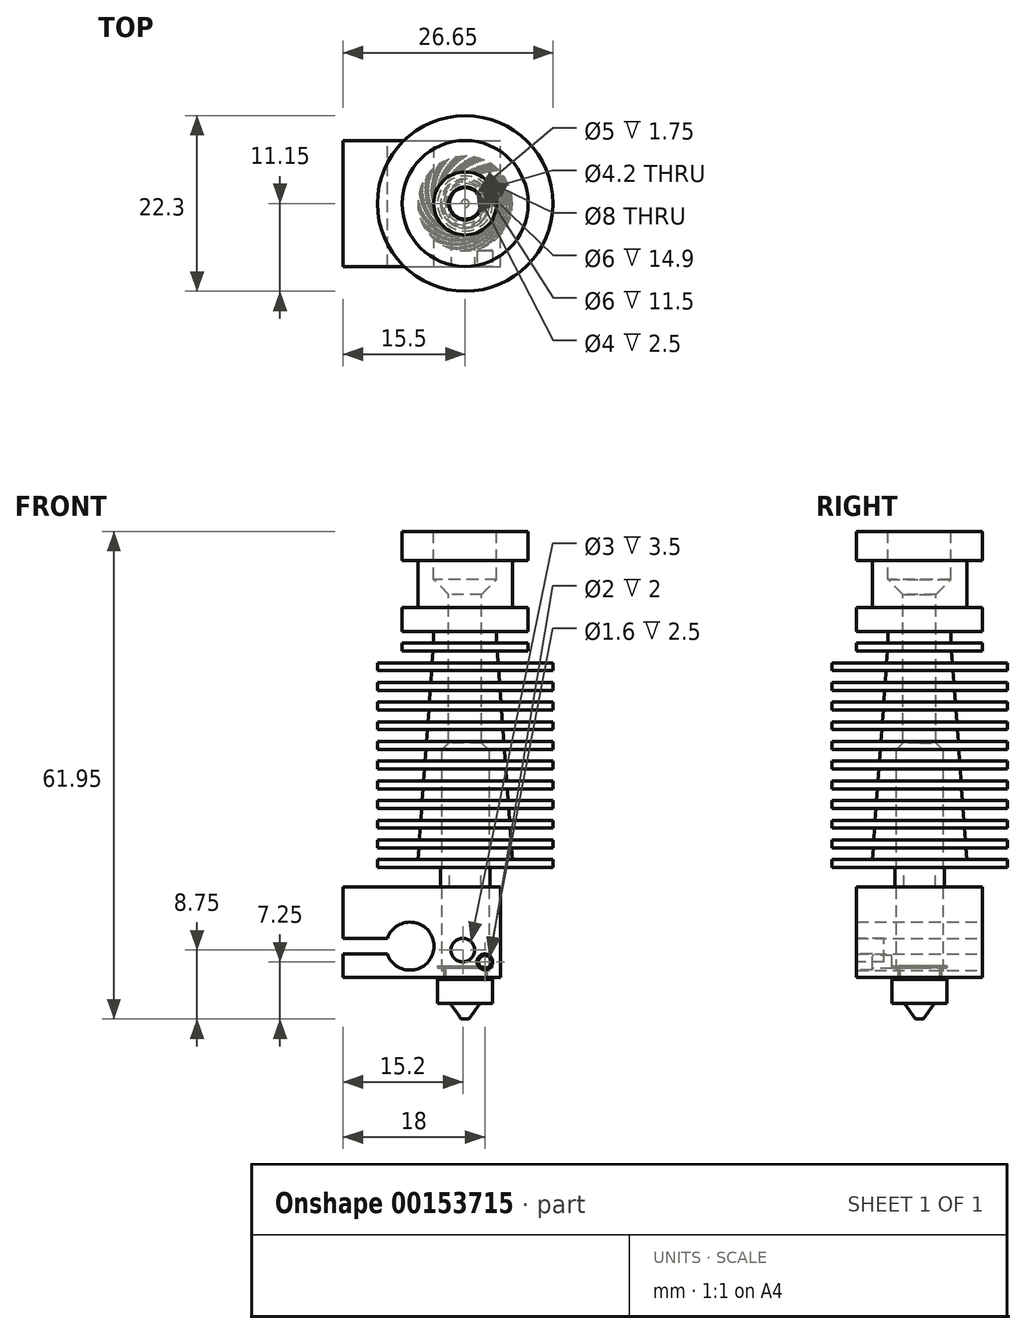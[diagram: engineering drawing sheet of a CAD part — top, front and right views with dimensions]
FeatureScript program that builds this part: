
annotation { "Feature Type Name" : "Feature", "Feature Type Description" : "" }
export const myFeature = defineFeature(function(context is Context, id is Id, definition is map)
    precondition{}
    {
        {
            var Q0;
            Q0=qCreatedBy(makeId("Top.planeOp"),FACE);
            var sketch = newSketch(context, id + "F0", { "sketchPlane" : qUnion([Q0])});
            skCircle(sketch, "E0", {"center": v(0, 0) * mm, "radius": 8 * mm});
            skSolve(sketch);
        }
        {
            var Q0;
            Q0=makeQuery(id+"F0.imprint","IMPRINT",FACE,{"disambiguationData":[TD([[makeQuery(id+"F0.imprint","IMPRINT",EDGE,{"derivedFrom":sQuery(id+"F0.wireOp",EDGE,"E0")}),1.0]])]});
            var Q1;
            Q1=sQuery(id+"F0.wireOp",EDGE,"E0");
            extrude(context, id + "F1", {"entities" : qUnion([Q0]), "surfaceEntities" : qUnion([Q1]), "oppositeDirection" : true, "depth" : 3.7 * mm});
        }
        {
            var Q0;
            Q0=makeQuery(id+"F1.opExtrude","CAP_FACE",FACE,{"disambiguationData":[OSD([sQuery(id+"F0.wireOp",EDGE,"E0")])],"isStart":false});
            var sketch = newSketch(context, id + "F2", { "sketchPlane" : qUnion([Q0])});
            skCircle(sketch, "E1", {"center": v(0, 0) * mm, "radius": 6 * mm});
            skSolve(sketch);
        }
        {
            var Q0;
            Q0=makeQuery(id+"F2.imprint","IMPRINT",FACE,{"disambiguationData":[TD([[makeQuery(id+"F2.imprint","IMPRINT",EDGE,{"derivedFrom":sQuery(id+"F2.wireOp",EDGE,"E1")}),1.0]])]});
            var Q1;
            Q1=sQuery(id+"F2.wireOp",EDGE,"E1");
            extrude(context, id + "F3", {"entities" : qUnion([Q0]), "operationType" : NewBodyOperationType.ADD, "surfaceEntities" : qUnion([Q1]), "depth" : 6 * mm});
        }
        {
            var Q0;
            Q0=makeQuery(id+"F3.opExtrude","CAP_FACE",FACE,{"disambiguationData":[OSD([sQuery(id+"F2.wireOp",EDGE,"E1")])],"isStart":false});
            var sketch = newSketch(context, id + "F4", { "sketchPlane" : qUnion([Q0])});
            skCircle(sketch, "E2", {"center": v(0, 0) * mm, "radius": 8 * mm});
            skSolve(sketch);
        }
        {
            var Q0;
            Q0=qSketchRegion(id+"F4",true);
            extrude(context, id + "F5", {"entities" : qUnion([Q0]), "operationType" : NewBodyOperationType.ADD, "depth" : 3 * mm});
        }
        {
            var Q0;
            Q0=qCreatedBy(makeId("Front.planeOp"),FACE);
            var sketch = newSketch(context, id + "F6", { "sketchPlane" : qUnion([Q0])});
            skLineSegment(sketch, "E3", {"start": v(0, 0) * mm, "end": v(0, -12.7) * mm});
            skLineSegment(sketch, "E4.bottom", {"start": v(0, -12.7) * mm, "end": v(4, -12.7) * mm});
            skLineSegment(sketch, "E4.top", {"start": v(0, -14.2) * mm, "end": v(4, -14.2) * mm});
            skLineSegment(sketch, "E4.left", {"start": v(0, -12.7) * mm, "end": v(0, -14.2) * mm});
            skLineSegment(sketch, "E4.right", {"start": v(4, -12.7) * mm, "end": v(4, -14.2) * mm});
            skLineSegment(sketch, "E5.bottom", {"start": v(0, -14.2) * mm, "end": v(8, -14.2) * mm});
            skLineSegment(sketch, "E5.top", {"start": v(0, -15.2) * mm, "end": v(8, -15.2) * mm});
            skLineSegment(sketch, "E5.left", {"start": v(0, -14.2) * mm, "end": v(0, -15.2) * mm});
            skLineSegment(sketch, "E5.right", {"start": v(8, -14.2) * mm, "end": v(8, -15.2) * mm});
            skLineSegment(sketch, "E6", {"start": v(0, -15.2) * mm, "end": v(0, -16.7) * mm});
            skLineSegment(sketch, "E7.bottom", {"start": v(0, -16.7) * mm, "end": v(11.15, -16.7) * mm});
            skLineSegment(sketch, "E7.top", {"start": v(0, -17.7) * mm, "end": v(11.15, -17.7) * mm});
            skLineSegment(sketch, "E7.left", {"start": v(0, -16.7) * mm, "end": v(0, -17.7) * mm});
            skLineSegment(sketch, "E7.right", {"start": v(11.15, -16.7) * mm, "end": v(11.15, -17.7) * mm});
            skLineSegment(sketch, "E8.1.0.0", {"start": v(0, -20.2) * mm, "end": v(11.15, -20.2) * mm});
            skLineSegment(sketch, "E8.1.0.1", {"start": v(0, -19.2) * mm, "end": v(11.15, -19.2) * mm});
            skLineSegment(sketch, "E8.1.0.2", {"start": v(0, -19.2) * mm, "end": v(0, -20.2) * mm});
            skLineSegment(sketch, "E8.1.0.3", {"start": v(11.15, -19.2) * mm, "end": v(11.15, -20.2) * mm});
            skLineSegment(sketch, "E8.2.0.0", {"start": v(0, -22.7) * mm, "end": v(11.15, -22.7) * mm});
            skLineSegment(sketch, "E8.2.0.1", {"start": v(0, -21.7) * mm, "end": v(11.15, -21.7) * mm});
            skLineSegment(sketch, "E8.2.0.2", {"start": v(0, -21.7) * mm, "end": v(0, -22.7) * mm});
            skLineSegment(sketch, "E8.2.0.3", {"start": v(11.15, -21.7) * mm, "end": v(11.15, -22.7) * mm});
            skLineSegment(sketch, "E8.3.0.0", {"start": v(0, -25.2) * mm, "end": v(11.15, -25.2) * mm});
            skLineSegment(sketch, "E8.3.0.1", {"start": v(0, -24.2) * mm, "end": v(11.15, -24.2) * mm});
            skLineSegment(sketch, "E8.3.0.2", {"start": v(0, -24.2) * mm, "end": v(0, -25.2) * mm});
            skLineSegment(sketch, "E8.3.0.3", {"start": v(11.15, -24.2) * mm, "end": v(11.15, -25.2) * mm});
            skLineSegment(sketch, "E8.4.0.0", {"start": v(0, -27.7) * mm, "end": v(11.15, -27.7) * mm});
            skLineSegment(sketch, "E8.4.0.1", {"start": v(0, -26.7) * mm, "end": v(11.15, -26.7) * mm});
            skLineSegment(sketch, "E8.4.0.2", {"start": v(0, -26.7) * mm, "end": v(0, -27.7) * mm});
            skLineSegment(sketch, "E8.4.0.3", {"start": v(11.15, -26.7) * mm, "end": v(11.15, -27.7) * mm});
            skLineSegment(sketch, "E8.5.0.0", {"start": v(0, -30.2) * mm, "end": v(11.15, -30.2) * mm});
            skLineSegment(sketch, "E8.5.0.1", {"start": v(0, -29.2) * mm, "end": v(11.15, -29.2) * mm});
            skLineSegment(sketch, "E8.5.0.2", {"start": v(0, -29.2) * mm, "end": v(0, -30.2) * mm});
            skLineSegment(sketch, "E8.5.0.3", {"start": v(11.15, -29.2) * mm, "end": v(11.15, -30.2) * mm});
            skLineSegment(sketch, "E8.6.0.0", {"start": v(0, -32.7) * mm, "end": v(11.15, -32.7) * mm});
            skLineSegment(sketch, "E8.6.0.1", {"start": v(0, -31.7) * mm, "end": v(11.15, -31.7) * mm});
            skLineSegment(sketch, "E8.6.0.2", {"start": v(0, -31.7) * mm, "end": v(0, -32.7) * mm});
            skLineSegment(sketch, "E8.6.0.3", {"start": v(11.15, -31.7) * mm, "end": v(11.15, -32.7) * mm});
            skLineSegment(sketch, "E8.7.0.0", {"start": v(0, -35.2) * mm, "end": v(11.15, -35.2) * mm});
            skLineSegment(sketch, "E8.7.0.1", {"start": v(0, -34.2) * mm, "end": v(11.15, -34.2) * mm});
            skLineSegment(sketch, "E8.7.0.2", {"start": v(0, -34.2) * mm, "end": v(0, -35.2) * mm});
            skLineSegment(sketch, "E8.7.0.3", {"start": v(11.15, -34.2) * mm, "end": v(11.15, -35.2) * mm});
            skLineSegment(sketch, "E8.8.0.0", {"start": v(0, -37.7) * mm, "end": v(11.15, -37.7) * mm});
            skLineSegment(sketch, "E8.8.0.1", {"start": v(0, -36.7) * mm, "end": v(11.15, -36.7) * mm});
            skLineSegment(sketch, "E8.8.0.2", {"start": v(0, -36.7) * mm, "end": v(0, -37.7) * mm});
            skLineSegment(sketch, "E8.8.0.3", {"start": v(11.15, -36.7) * mm, "end": v(11.15, -37.7) * mm});
            skLineSegment(sketch, "E8.9.0.0", {"start": v(0, -40.2) * mm, "end": v(11.15, -40.2) * mm});
            skLineSegment(sketch, "E8.9.0.1", {"start": v(0, -39.2) * mm, "end": v(11.15, -39.2) * mm});
            skLineSegment(sketch, "E8.9.0.2", {"start": v(0, -39.2) * mm, "end": v(0, -40.2) * mm});
            skLineSegment(sketch, "E8.9.0.3", {"start": v(11.15, -39.2) * mm, "end": v(11.15, -40.2) * mm});
            skLineSegment(sketch, "E8.10.0.0", {"start": v(0, -42.7) * mm, "end": v(11.15, -42.7) * mm});
            skLineSegment(sketch, "E8.10.0.1", {"start": v(0, -41.7) * mm, "end": v(11.15, -41.7) * mm});
            skLineSegment(sketch, "E8.10.0.2", {"start": v(0, -41.7) * mm, "end": v(0, -42.7) * mm});
            skLineSegment(sketch, "E8.10.0.3", {"start": v(11.15, -41.7) * mm, "end": v(11.15, -42.7) * mm});
            skLineSegment(sketch, "E8.direction1", {"start": v(0, -17.7) * mm, "end": v(0, -20.2) * mm, "construction": true});
            skLineSegment(sketch, "E9", {"start": v(0, -41.7) * mm, "end": v(6, -41.7) * mm});
            skLineSegment(sketch, "E10", {"start": v(4.07, -15.2) * mm, "end": v(4.18, -16.7) * mm});
            skLineSegment(sketch, "E11.trimOffspring", {"start": v(4.25, -17.7) * mm, "end": v(4.36, -19.2) * mm});
            skLineSegment(sketch, "E12.trimOffspring", {"start": v(4.44, -20.2) * mm, "end": v(4.55, -21.7) * mm});
            skLineSegment(sketch, "E13.trimOffspring", {"start": v(4.62, -22.7) * mm, "end": v(4.73, -24.2) * mm});
            skLineSegment(sketch, "E14.trimOffspring", {"start": v(4.8, -25.2) * mm, "end": v(4.9, -26.7) * mm});
            skLineSegment(sketch, "E15.trimOffspring", {"start": v(4.98, -27.7) * mm, "end": v(5.1, -29.2) * mm});
            skLineSegment(sketch, "E16.trimOffspring", {"start": v(5.16, -30.2) * mm, "end": v(5.27, -31.7) * mm});
            skLineSegment(sketch, "E17.trimOffspring", {"start": v(5.35, -32.7) * mm, "end": v(5.45, -34.2) * mm});
            skLineSegment(sketch, "E18.trimOffspring", {"start": v(5.53, -35.2) * mm, "end": v(5.64, -36.7) * mm});
            skLineSegment(sketch, "E19.trimOffspring", {"start": v(5.7, -37.7) * mm, "end": v(5.82, -39.2) * mm});
            skLineSegment(sketch, "E20.trimOffspring", {"start": v(5.9, -40.2) * mm, "end": v(6, -41.7) * mm});
            skLineSegment(sketch, "E21", {"start": v(0, -17.7) * mm, "end": v(0, -19.2) * mm});
            skLineSegment(sketch, "E22", {"start": v(0, -20.2) * mm, "end": v(0, -21.7) * mm});
            skLineSegment(sketch, "E23", {"start": v(0, -22.7) * mm, "end": v(0, -24.2) * mm});
            skLineSegment(sketch, "E24", {"start": v(0, -25.2) * mm, "end": v(0, -26.7) * mm});
            skLineSegment(sketch, "E25", {"start": v(0, -27.7) * mm, "end": v(0, -29.2) * mm});
            skLineSegment(sketch, "E26", {"start": v(0, -30.2) * mm, "end": v(0, -31.7) * mm});
            skLineSegment(sketch, "E27", {"start": v(0, -32.7) * mm, "end": v(0, -34.2) * mm});
            skLineSegment(sketch, "E28", {"start": v(0, -35.2) * mm, "end": v(0, -36.7) * mm});
            skLineSegment(sketch, "E29", {"start": v(0, -37.7) * mm, "end": v(0, -39.2) * mm});
            skLineSegment(sketch, "E30", {"start": v(0, -40.2) * mm, "end": v(0, -41.7) * mm});
            skLineSegment(sketch, "E31.right", {"start": v(3, -42.7) * mm, "end": v(3, -45.2) * mm});
            skLineSegment(sketch, "E32", {"start": v(3, -45.2) * mm, "end": v(2, -45.2) * mm});
            skLineSegment(sketch, "E33", {"start": v(2, -45.2) * mm, "end": v(2, -42.7) * mm});
            skLineSegment(sketch, "E34.bottom", {"start": v(2, -45.2) * mm, "end": v(3, -45.2) * mm});
            skLineSegment(sketch, "E34.top", {"start": v(2, -47.3) * mm, "end": v(3, -47.3) * mm});
            skLineSegment(sketch, "E34.left", {"start": v(2, -45.2) * mm, "end": v(2, -47.3) * mm});
            skLineSegment(sketch, "E34.right", {"start": v(3, -45.2) * mm, "end": v(3, -47.3) * mm});
            skLineSegment(sketch, "E35.bottom", {"start": v(3, -47.3) * mm, "end": v(3.75, -47.3) * mm});
            skLineSegment(sketch, "E35.top", {"start": v(3, -46.56) * mm, "end": v(3.75, -46.56) * mm});
            skLineSegment(sketch, "E35.left", {"start": v(3, -47.3) * mm, "end": v(3, -46.56) * mm});
            skLineSegment(sketch, "E35.right", {"start": v(3.75, -47.3) * mm, "end": v(3.75, -46.56) * mm});
            skLineSegment(sketch, "E36.bottom", {"start": v(2, -42.7) * mm, "end": v(3, -42.7) * mm});
            skLineSegment(sketch, "E36.top", {"start": v(2, -41.7) * mm, "end": v(3, -41.7) * mm});
            skLineSegment(sketch, "E36.left", {"start": v(2, -42.7) * mm, "end": v(2, -41.7) * mm});
            skLineSegment(sketch, "E36.right", {"start": v(3, -42.7) * mm, "end": v(3, -41.7) * mm});
            skSolve(sketch);
        }
        {
            var Q0;
            Q0=qSketchRegion(id+"F6",true);
            var Q1;
            {var subQ0=sQuery(id+"F6.wireOp",EDGE,"E31.right");Q1=makeQuery(id+"F6.imprint","IMPRINT",FACE,{"disambiguationData":[TD([[makeQuery(id+"F6.imprint","IMPRINT",EDGE,{"derivedFrom":subQ0}),-1.0]])]});}
            var Q2;
            Q2=makeQuery(id+"F6.imprint","IMPRINT",FACE,{"disambiguationData":[TD([[makeQuery(id+"F6.imprint","IMPRINT",EDGE,{"derivedFrom":sQuery(id+"F6.wireOp",EDGE,"E34.bottom")}),-1.0]])]});
            var Q3;
            Q3=makeQuery(id+"F6.imprint","IMPRINT",FACE,{"disambiguationData":[TD([[makeQuery(id+"F6.imprint","IMPRINT",EDGE,{"derivedFrom":sQuery(id+"F6.wireOp",EDGE,"E36.bottom")}),1.0]])]});
            var Q4;
            Q4=makeQuery(id+"F6.imprint","IMPRINT",FACE,{"disambiguationData":[TD([[makeQuery(id+"F6.imprint","IMPRINT",EDGE,{"derivedFrom":sQuery(id+"F6.wireOp",EDGE,"E31.right")}),-1.0]])]});
            var Q5;
            Q5=makeQuery(id+"F6.imprint","IMPRINT",FACE,{"disambiguationData":[TD([[makeQuery(id+"F6.imprint","IMPRINT",EDGE,{"derivedFrom":sQuery(id+"F6.wireOp",EDGE,"E34.bottom")}),-1.0]])]});
            var Q6;
            Q6=sQuery(id+"F6.wireOp",EDGE,"E3");
            revolve(context, id + "F7", {"operationType" : NewBodyOperationType.ADD, "entities" : qUnion([Q0, Q1, Q2, Q3, Q4, Q5]), "axis" : qUnion([Q6]), "revolveType" : RevolveType.FULL});
        }
        {
            var Q0;
            Q0=makeQuery(id+"F1.opExtrude","CAP_FACE",FACE,{"disambiguationData":[OSD([sQuery(id+"F0.wireOp",EDGE,"E0")])],"isStart":true});
            var sketch = newSketch(context, id + "F8", { "sketchPlane" : qUnion([Q0])});
            skCircle(sketch, "E37", {"center": v(0, 0) * mm, "radius": 2.1 * mm});
            skSolve(sketch);
        }
        {
            var Q0;
            Q0=qSketchRegion(id+"F8",true);
            extrude(context, id + "F9", {"entities" : qUnion([Q0]), "operationType" : NewBodyOperationType.REMOVE, "oppositeDirection" : true, "depth" : 42.7 * mm});
        }
        {
            var Q0;
            Q0=makeQuery(id+"F1.opExtrude","CAP_FACE",FACE,{"disambiguationData":[OSD([sQuery(id+"F0.wireOp",EDGE,"E0")])],"isStart":true});
            var sketch = newSketch(context, id + "F10", { "sketchPlane" : qUnion([Q0])});
            skCircle(sketch, "E38", {"center": v(0, 0) * mm, "radius": 4 * mm});
            skSolve(sketch);
        }
        {
            var Q0;
            Q0=qSketchRegion(id+"F10",true);
            extrude(context, id + "F11", {"entities" : qUnion([Q0]), "operationType" : NewBodyOperationType.REMOVE, "oppositeDirection" : true, "depth" : 6 * mm});
        }
        {
            var Q0;
            Q0=makeQuery(id+"F11.boolean.opBoolean","INTERSECT",EDGE,{"derivedFrom":[makeQuery(id+"F9.boolean.opBoolean","COPY",FACE,{"derivedFrom":makeQuery(id+"F9.opExtrude","SWEPT_FACE",FACE,{"disambiguationData":[OSD([sQuery(id+"F8.wireOp",EDGE,"E37")])]})}),makeQuery(id+"F11.opExtrude","CAP_FACE",FACE,{"disambiguationData":[OSD([sQuery(id+"F10.wireOp",EDGE,"E38")])],"isStart":false})]});
            chamfer(context, id + "F12", {"entities" : qUnion([Q0]), "width" : 2 * mm, "tangentPropagation" : true});
        }
        {
            var Q0;
            Q0=makeQuery(id+"F7.opRevolve","SWEPT_FACE",FACE,{"disambiguationData":[OSD([sQuery(id+"F6.wireOp",EDGE,"E8.10.0.0")])]});
            var sketch = newSketch(context, id + "F13", { "sketchPlane" : qUnion([Q0])});
            skCircle(sketch, "E39", {"center": v(0, 0) * mm, "radius": 3 * mm});
            skSolve(sketch);
        }
        {
            var Q0;
            Q0=qSketchRegion(id+"F13",true);
            extrude(context, id + "F14", {"entities" : qUnion([Q0]), "operationType" : NewBodyOperationType.REMOVE, "oppositeDirection" : true, "depth" : 14.8 * mm});
        }
        {
            var Q0;
            Q0=makeQuery(id+"F14.boolean.opBoolean","INTERSECT",EDGE,{"derivedFrom":[makeQuery(id+"F9.boolean.opBoolean","COPY",FACE,{"derivedFrom":makeQuery(id+"F9.opExtrude","SWEPT_FACE",FACE,{"disambiguationData":[OSD([sQuery(id+"F8.wireOp",EDGE,"E37")])]})}),makeQuery(id+"F14.opExtrude","CAP_FACE",FACE,{"disambiguationData":[OSD([sQuery(id+"F13.wireOp",EDGE,"E39")])],"isStart":false})]});
            chamfer(context, id + "F15", {"entities" : qUnion([Q0]), "width" : 1 * mm, "tangentPropagation" : true});
        }
        {
            var Q0;
            Q0=qCreatedBy(makeId("Front.planeOp"),FACE);
            var sketch = newSketch(context, id + "F16", { "sketchPlane" : qUnion([Q0])});
            skLineSegment(sketch, "E40.bottom", {"start": v(-15.5, -45.2) * mm, "end": v(4.5, -45.2) * mm});
            skLineSegment(sketch, "E40.top", {"start": v(-15.5, -56.7) * mm, "end": v(4.5, -56.7) * mm});
            skLineSegment(sketch, "E40.left", {"start": v(-15.5, -45.2) * mm, "end": v(-15.5, -51.7) * mm});
            skLineSegment(sketch, "E40.right", {"start": v(4.5, -45.2) * mm, "end": v(4.5, -56.7) * mm});
            skArc(sketch, "E41", {"start": v(-9.88, -53.7) * mm, "mid": v(-3.95, -52.7) * mm, "end": v(-9.88, -51.7) * mm});
            skLineSegment(sketch, "E42.top", {"start": v(-15.5, -51.7) * mm, "end": v(-9.88, -51.7) * mm});
            skLineSegment(sketch, "E43.top", {"start": v(-15.5, -53.7) * mm, "end": v(-9.88, -53.7) * mm});
            skLineSegment(sketch, "E44.trimOffspring", {"start": v(-15.5, -53.7) * mm, "end": v(-15.5, -56.7) * mm});
            skSolve(sketch);
        }
        {
            var Q0;
            Q0=makeQuery(id+"F16.imprint","IMPRINT",FACE,{"disambiguationData":[TD([[makeQuery(id+"F16.imprint","IMPRINT",EDGE,{"derivedFrom":sQuery(id+"F16.wireOp",EDGE,"E40.bottom")}),-1.0]])]});
            var Q1;
            Q1=makeQuery(id+"F16.imprint","IMPRINT",FACE,{"disambiguationData":[TD([[makeQuery(id+"F16.imprint","IMPRINT",EDGE,{"derivedFrom":sQuery(id+"F16.wireOp",EDGE,"hSTLO5rz-Z077-ZaO5-nEVS-phWlFBx8dYmu")}),1.0]])]});
            var Q2;
            Q2=makeQuery(id+"F16.imprint","IMPRINT",FACE,{"disambiguationData":[TD([[makeQuery(id+"F16.imprint","IMPRINT",EDGE,{"derivedFrom":sQuery(id+"F16.wireOp",EDGE,"1ucrc5hz-Jwvr-DOmE-K7qY-mdj6J8iSEPF0")}),1.0]])]});
            extrude(context, id + "F17", {"entities" : qUnion([Q0, Q1, Q2]), "endBound" : BoundingType.SYMMETRIC, "depth" : 16 * mm});
        }
        {
            var Q0;
            Q0=makeQuery(id+"F17.opExtrude","SWEPT_FACE",FACE,{"disambiguationData":[OSD([sQuery(id+"F16.wireOp",EDGE,"E40.top")])]});
            var sketch = newSketch(context, id + "F18", { "sketchPlane" : qUnion([Q0])});
            skCircle(sketch, "E45", {"center": v(0, 0) * mm, "radius": 3 * mm});
            skSolve(sketch);
        }
        {
            var Q0;
            Q0=qSketchRegion(id+"F18",true);
            extrude(context, id + "F19", {"entities" : qUnion([Q0]), "operationType" : NewBodyOperationType.REMOVE, "oppositeDirection" : true, "depth" : 11.5 * mm});
        }
        {
            var Q0;
            Q0=qCreatedBy(makeId("Front.planeOp"),FACE);
            var sketch = newSketch(context, id + "F20", { "sketchPlane" : qUnion([Q0])});
            skLineSegment(sketch, "E46.bottom", {"start": v(0, -56.95) * mm, "end": v(3.5, -56.95) * mm});
            skLineSegment(sketch, "E46.right", {"start": v(3.5, -56.95) * mm, "end": v(3.5, -59.95) * mm});
            skLineSegment(sketch, "E47.top", {"start": v(0, -61.95) * mm, "end": v(0.5, -61.95) * mm});
            skLineSegment(sketch, "E48", {"start": v(0.5, -61.95) * mm, "end": v(1.9, -59.95) * mm});
            skLineSegment(sketch, "E49.trimOffspring", {"start": v(1.9, -59.95) * mm, "end": v(3.5, -59.95) * mm});
            skLineSegment(sketch, "E50", {"start": v(0, -61.95) * mm, "end": v(0, -56.95) * mm});
            skLineSegment(sketch, "E51", {"start": v(0, -56.95) * mm, "end": v(2.5, -56.95) * mm});
            skLineSegment(sketch, "E52", {"start": v(2.5, -56.95) * mm, "end": v(2.5, -55.45) * mm});
            skLineSegment(sketch, "E53", {"start": v(2.5, -55.45) * mm, "end": v(2.75, -55.45) * mm});
            skLineSegment(sketch, "E54", {"start": v(2.75, -55.45) * mm, "end": v(2.75, -56.95) * mm});
            skLineSegment(sketch, "E55.bottom", {"start": v(2.5, -55.45) * mm, "end": v(3.5, -55.45) * mm});
            skLineSegment(sketch, "E55.top", {"start": v(2.5, -55.2) * mm, "end": v(3.5, -55.2) * mm});
            skLineSegment(sketch, "E55.left", {"start": v(2.5, -55.45) * mm, "end": v(2.5, -55.2) * mm});
            skLineSegment(sketch, "E55.right", {"start": v(3.5, -55.45) * mm, "end": v(3.5, -55.2) * mm});
            skSolve(sketch);
        }
        {
            var Q0;
            Q0=qSketchRegion(id+"F20",true);
            var Q1;
            Q1=sQuery(id+"F20.wireOp",EDGE,"E50");
            revolve(context, id + "F21", {"entities" : qUnion([Q0]), "axis" : qUnion([Q1]), "revolveType" : RevolveType.FULL});
        }
        {
            var Q0;
            Q0=makeQuery(id+"F17.opExtrude","CAP_FACE",FACE,{"disambiguationData":[OSD([sQuery(id+"F16.wireOp",EDGE,"E40.bottom"),sQuery(id+"F16.wireOp",EDGE,"E40.top"),sQuery(id+"F16.wireOp",EDGE,"E40.left"),sQuery(id+"F16.wireOp",EDGE,"E40.right"),sQuery(id+"F16.wireOp",EDGE,"E41"),sQuery(id+"F16.wireOp",EDGE,"E42.top"),sQuery(id+"F16.wireOp",EDGE,"E43.top"),sQuery(id+"F16.wireOp",EDGE,"E44.trimOffspring")])],"isStart":false});
            var sketch = newSketch(context, id + "F22", { "sketchPlane" : qUnion([Q0])});
            skCircle(sketch, "E56", {"center": v(-0.3, -53.2) * mm, "radius": 1.5 * mm});
            skCircle(sketch, "E57", {"center": v(2.5, -54.7) * mm, "radius": 1 * mm});
            skCircle(sketch, "E58", {"center": v(2.5, -54.7) * mm, "radius": 0.8 * mm});
            skSolve(sketch);
        }
        {
            var Q0;
            Q0=makeQuery(id+"F22.imprint","IMPRINT",FACE,{"disambiguationData":[TD([[makeQuery(id+"F22.imprint","IMPRINT",EDGE,{"derivedFrom":sQuery(id+"F22.wireOp",EDGE,"E56")}),1.0]])]});
            extrude(context, id + "F23", {"entities" : qUnion([Q0]), "operationType" : NewBodyOperationType.REMOVE, "oppositeDirection" : true, "depth" : 3.5 * mm});
        }
        {
            var Q0;
            Q0=makeQuery(id+"F22.imprint","IMPRINT",FACE,{"disambiguationData":[TD([[makeQuery(id+"F22.imprint","IMPRINT",EDGE,{"derivedFrom":sQuery(id+"F22.wireOp",EDGE,"E57")}),1.0]])]});
            extrude(context, id + "F24", {"entities" : qUnion([Q0]), "operationType" : NewBodyOperationType.REMOVE, "oppositeDirection" : true, "depth" : 2 * mm});
        }
        {
            var Q0;
            Q0=makeQuery(id+"F22.imprint","IMPRINT",FACE,{"disambiguationData":[TD([[makeQuery(id+"F22.imprint","IMPRINT",EDGE,{"derivedFrom":sQuery(id+"F22.wireOp",EDGE,"E58")}),1.0]])]});
            extrude(context, id + "F25", {"entities" : qUnion([Q0]), "operationType" : NewBodyOperationType.REMOVE, "oppositeDirection" : true, "depth" : 4.5 * mm});
        }
        {
            var Q0;
            {var subQ0=sQuery(id+"F6.wireOp",EDGE,"E8.10.0.0");Q0=makeQuery(id+"F7.opRevolve","SWEPT_FACE",FACE,{"disambiguationData":[OSD([subQ0]),TDD([makeQuery(id+"F6.imprint","IMPRINT",EDGE,{"disambiguationData":[TD([[makeQuery(id+"F6.imprint","INTERSECT",VERTEX,{"derivedFrom":[subQ0,sQuery(id+"F6.wireOp",EDGE,"E8.10.0.3")]}),1.0]])],"derivedFrom":subQ0})])]});}
            var sketch = newSketch(context, id + "F26", { "sketchPlane" : qUnion([Q0])});
            skCircle(sketch, "E59", {"center": v(0, 0) * mm, "radius": 3.12 * mm});
            skSolve(sketch);
        }
        {
            var Q0;
            Q0=makeQuery(id+"F26.imprint","IMPRINT",FACE,{"disambiguationData":[TD([[makeQuery(id+"F26.imprint","IMPRINT",EDGE,{"derivedFrom":sQuery(id+"F26.wireOp",EDGE,"E59")}),1.0]])]});
            extrude(context, id + "F27", {"entities" : qUnion([Q0]), "operationType" : NewBodyOperationType.ADD, "depth" : 5 * mm});
        }
    });
